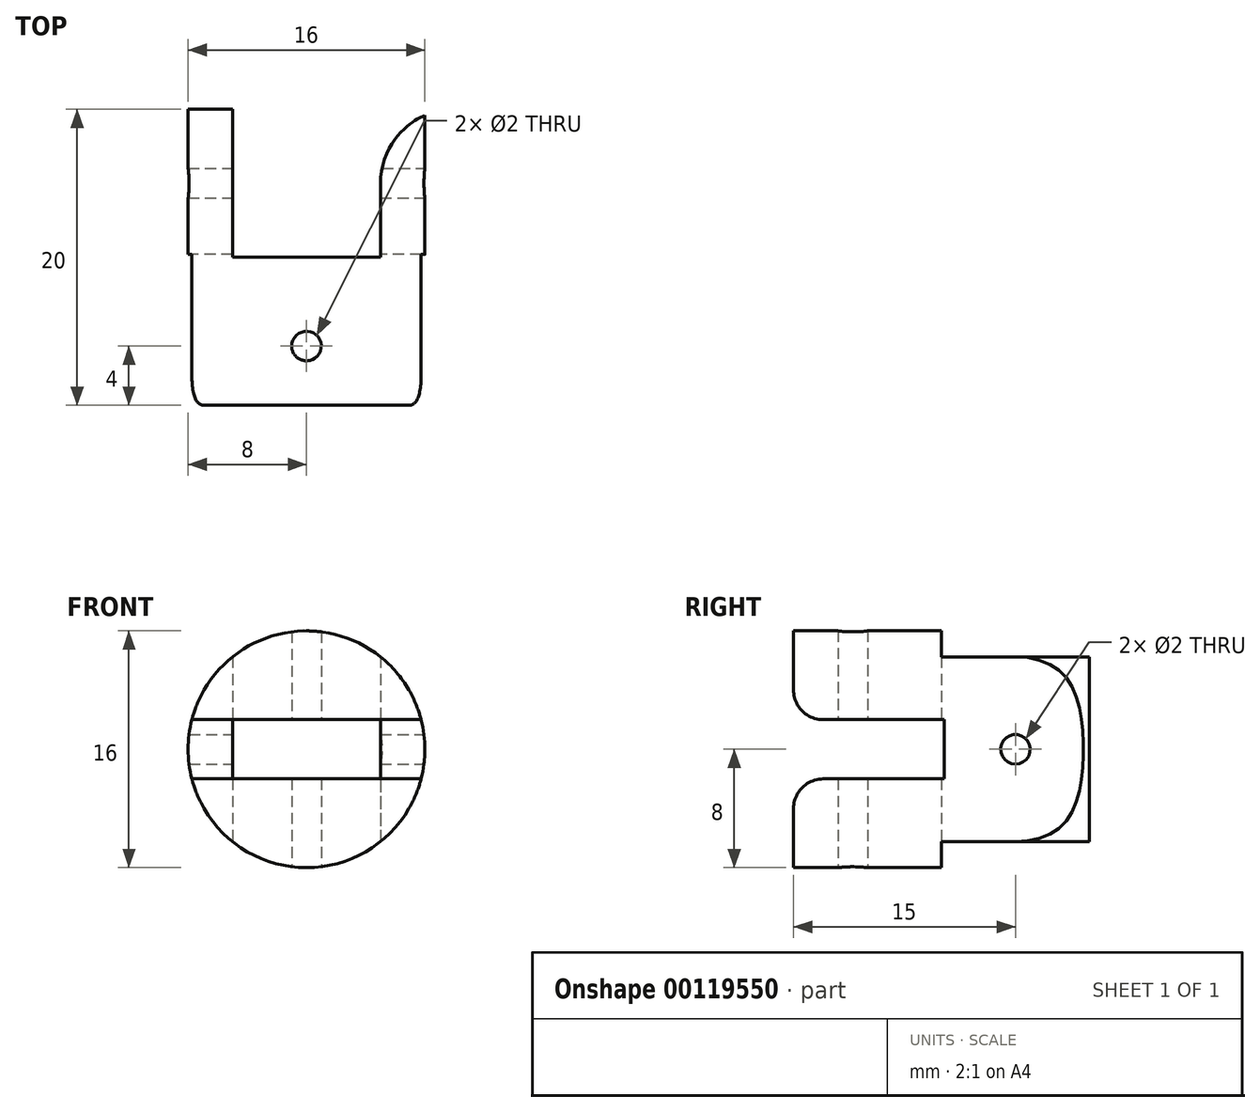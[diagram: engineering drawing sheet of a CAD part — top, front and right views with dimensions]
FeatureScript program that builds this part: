
annotation { "Feature Type Name" : "Feature", "Feature Type Description" : "" }
export const myFeature = defineFeature(function(context is Context, id is Id, definition is map)
    precondition{}
    {
        {
            var Q0;
            Q0=qCreatedBy(makeId("Front.planeOp"),FACE);
            var sketch = newSketch(context, id + "F0", { "sketchPlane" : qUnion([Q0])});
            skCircle(sketch, "E0", {"center": v(0, 0) * mm, "radius": 8 * mm});
            skSolve(sketch);
        }
        {
            var Q0;
            Q0=makeQuery(id+"F0.imprint","IMPRINT",FACE,{"disambiguationData":[TD([[makeQuery(id+"F0.imprint","IMPRINT",EDGE,{"derivedFrom":sQuery(id+"F0.wireOp",EDGE,"E0")}),1.0]])]});
            extrude(context, id + "F1", {"entities" : qUnion([Q0]), "depth" : 20 * mm});
        }
        {
            var Q0;
            Q0=qCreatedBy(makeId("Front.planeOp"),FACE);
            var sketch = newSketch(context, id + "F2", { "sketchPlane" : qUnion([Q0])});
            skLineSegment(sketch, "E1.bottom", {"start": v(-5, 10.24) * mm, "end": v(5, 10.24) * mm});
            skLineSegment(sketch, "E1.top", {"start": v(-5, -10.24) * mm, "end": v(5, -10.24) * mm});
            skLineSegment(sketch, "E1.left", {"start": v(-5, 10.24) * mm, "end": v(-5, -10.24) * mm});
            skLineSegment(sketch, "E1.right", {"start": v(5, 10.24) * mm, "end": v(5, -10.24) * mm});
            skPoint(sketch, "E1.middle", {"position": v(0, 0) * mm});
            skSolve(sketch);
        }
        {
            var Q0;
            Q0=makeQuery(id+"F2.imprint","IMPRINT",FACE,{"disambiguationData":[TD([[makeQuery(id+"F2.imprint","IMPRINT",EDGE,{"derivedFrom":sQuery(id+"F2.wireOp",EDGE,"E1.bottom")}),-1.0]])]});
            extrude(context, id + "F3", {"entities" : qUnion([Q0]), "operationType" : NewBodyOperationType.REMOVE, "depth" : 10 * mm});
        }
        {
            var Q0;
            Q0=qCreatedBy(makeId("Right.planeOp"),FACE);
            var sketch = newSketch(context, id + "F4", { "sketchPlane" : qUnion([Q0])});
            skLineSegment(sketch, "E2.bottom", {"start": v(-9.81, 2) * mm, "end": v(-29.81, 2) * mm});
            skLineSegment(sketch, "E2.top", {"start": v(-9.81, -2) * mm, "end": v(-29.81, -2) * mm});
            skLineSegment(sketch, "E2.left", {"start": v(-9.81, 2) * mm, "end": v(-9.81, -2) * mm});
            skLineSegment(sketch, "E2.right", {"start": v(-29.81, 2) * mm, "end": v(-29.81, -2) * mm});
            skPoint(sketch, "E2.middle", {"position": v(-19.81, 0) * mm});
            skSolve(sketch);
        }
        {
            var Q0;
            Q0=makeQuery(id+"F4.imprint","IMPRINT",FACE,{"disambiguationData":[TD([[makeQuery(id+"F4.imprint","IMPRINT",EDGE,{"derivedFrom":sQuery(id+"F4.wireOp",EDGE,"E2.bottom")}),1.0]])]});
            extrude(context, id + "F5", {"entities" : qUnion([Q0]), "operationType" : NewBodyOperationType.REMOVE, "endBound" : BoundingType.SYMMETRIC, "depth" : 100 * mm});
        }
        {
            var Q0;
            Q0=makeQuery(id+"F3.boolean.opBoolean","COPY",EDGE,{"derivedFrom":makeQuery(id+"F3.opExtrude","CAP_EDGE",EDGE,{"disambiguationData":[OSD([sQuery(id+"F2.wireOp",EDGE,"E1.right")])],"isStart":true})});
            var Q1;
            Q1=makeQuery(id+"F3.boolean.opBoolean","COPY",EDGE,{"derivedFrom":makeQuery(id+"F3.opExtrude","CAP_EDGE",EDGE,{"disambiguationData":[OSD([sQuery(id+"F2.wireOp",EDGE,"E1.left")])],"isStart":true})});
            fillet(context, id + "F6", {"entities" : qUnion([Q0, Q1]), "radius" : 5 * mm, "tangentPropagation" : true, "allowEdgeOverflow" : false});
        }
        {
            var Q0;
            Q0=makeQuery(id+"F5.boolean.opBoolean","INTERSECT",EDGE,{"derivedFrom":[makeQuery(id+"F1.opExtrude","CAP_FACE",FACE,{"disambiguationData":[OSD([sQuery(id+"F0.wireOp",EDGE,"E0")])],"isStart":false}),makeQuery(id+"F5.opExtrude","SWEPT_FACE",FACE,{"disambiguationData":[OSD([sQuery(id+"F4.wireOp",EDGE,"E2.top")])]})]});
            var Q1;
            Q1=makeQuery(id+"F5.boolean.opBoolean","INTERSECT",EDGE,{"derivedFrom":[makeQuery(id+"F1.opExtrude","CAP_FACE",FACE,{"disambiguationData":[OSD([sQuery(id+"F0.wireOp",EDGE,"E0")])],"isStart":false}),makeQuery(id+"F5.opExtrude","SWEPT_FACE",FACE,{"disambiguationData":[OSD([sQuery(id+"F4.wireOp",EDGE,"E2.bottom")])]})]});
            fillet(context, id + "F7", {"entities" : qUnion([Q0, Q1]), "radius" : 2 * mm, "tangentPropagation" : true, "allowEdgeOverflow" : false});
        }
        {
            var Q0;
            Q0=makeQuery(id+"F3.boolean.opBoolean","COPY",FACE,{"derivedFrom":makeQuery(id+"F3.opExtrude","SWEPT_FACE",FACE,{"disambiguationData":[OSD([sQuery(id+"F2.wireOp",EDGE,"E1.left")])]})});
            var sketch = newSketch(context, id + "F8", { "sketchPlane" : qUnion([Q0])});
            skCircle(sketch, "E3", {"center": v(-5, 0) * mm, "radius": 1 * mm});
            skSolve(sketch);
        }
        {
            var Q0;
            {var subQ0=sQuery(id+"F8.wireOp",EDGE,"E3");var subQ1=sQuery(id+"F2.wireOp",EDGE,"E1.left");var subQ2=makeQuery(id+"F6.opFillet","BLEND_EDGE",EDGE,{"blendedFrom":[makeQuery(id+"F3.boolean.opBoolean","COPY",EDGE,{"derivedFrom":makeQuery(id+"F3.opExtrude","CAP_EDGE",EDGE,{"disambiguationData":[OSD([subQ1])],"isStart":true})}),makeQuery(id+"F3.boolean.opBoolean","COPY",FACE,{"derivedFrom":makeQuery(id+"F3.opExtrude","SWEPT_FACE",FACE,{"disambiguationData":[OSD([subQ1])]})})],"blendedInto":[makeQuery(id+"F3.boolean.opBoolean","COPY",FACE,{"derivedFrom":makeQuery(id+"F3.opExtrude","SWEPT_FACE",FACE,{"disambiguationData":[OSD([subQ1])]})})]});var subQ3=makeQuery(id+"F8.imprint","INTERSECT",VERTEX,{"disambiguationData":[OD(0.0)],"derivedFrom":[subQ2,subQ0]});Q0=makeQuery(id+"F8.imprint","IMPRINT",FACE,{"disambiguationData":[TD([[makeQuery(id+"F8.imprint","IMPRINT",EDGE,{"disambiguationData":[TD([[subQ3,1.0]])],"derivedFrom":subQ0}),1.0]])]});}
            var Q1;
            {var subQ0=sQuery(id+"F8.wireOp",EDGE,"E3");var subQ1=sQuery(id+"F2.wireOp",EDGE,"E1.left");var subQ2=makeQuery(id+"F6.opFillet","BLEND_EDGE",EDGE,{"blendedFrom":[makeQuery(id+"F3.boolean.opBoolean","COPY",EDGE,{"derivedFrom":makeQuery(id+"F3.opExtrude","CAP_EDGE",EDGE,{"disambiguationData":[OSD([subQ1])],"isStart":true})}),makeQuery(id+"F3.boolean.opBoolean","COPY",FACE,{"derivedFrom":makeQuery(id+"F3.opExtrude","SWEPT_FACE",FACE,{"disambiguationData":[OSD([subQ1])]})})],"blendedInto":[makeQuery(id+"F3.boolean.opBoolean","COPY",FACE,{"derivedFrom":makeQuery(id+"F3.opExtrude","SWEPT_FACE",FACE,{"disambiguationData":[OSD([subQ1])]})})]});var subQ3=makeQuery(id+"F8.imprint","INTERSECT",VERTEX,{"disambiguationData":[OD(0.0)],"derivedFrom":[subQ2,subQ0]});Q1=makeQuery(id+"F8.imprint","IMPRINT",FACE,{"disambiguationData":[TD([[makeQuery(id+"F8.imprint","IMPRINT",EDGE,{"disambiguationData":[TD([[subQ3,-1.0]])],"derivedFrom":subQ0}),1.0]])]});}
            extrude(context, id + "F9", {"entities" : qUnion([Q0, Q1]), "operationType" : NewBodyOperationType.REMOVE, "endBound" : BoundingType.SYMMETRIC, "oppositeDirection" : true, "depth" : 100 * mm});
        }
        {
            var Q0;
            Q0=qCreatedBy(makeId("Top.planeOp"),FACE);
            var sketch = newSketch(context, id + "F10", { "sketchPlane" : qUnion([Q0])});
            skCircle(sketch, "E4", {"center": v(0, -16) * mm, "radius": 1 * mm});
            skSolve(sketch);
        }
        {
            var Q0;
            Q0=makeQuery(id+"F10.imprint","IMPRINT",FACE,{"disambiguationData":[TD([[makeQuery(id+"F10.imprint","IMPRINT",EDGE,{"derivedFrom":sQuery(id+"F10.wireOp",EDGE,"E4")}),1.0]])]});
            extrude(context, id + "F11", {"entities" : qUnion([Q0]), "operationType" : NewBodyOperationType.REMOVE, "endBound" : BoundingType.SYMMETRIC, "depth" : 50 * mm});
        }
    });
